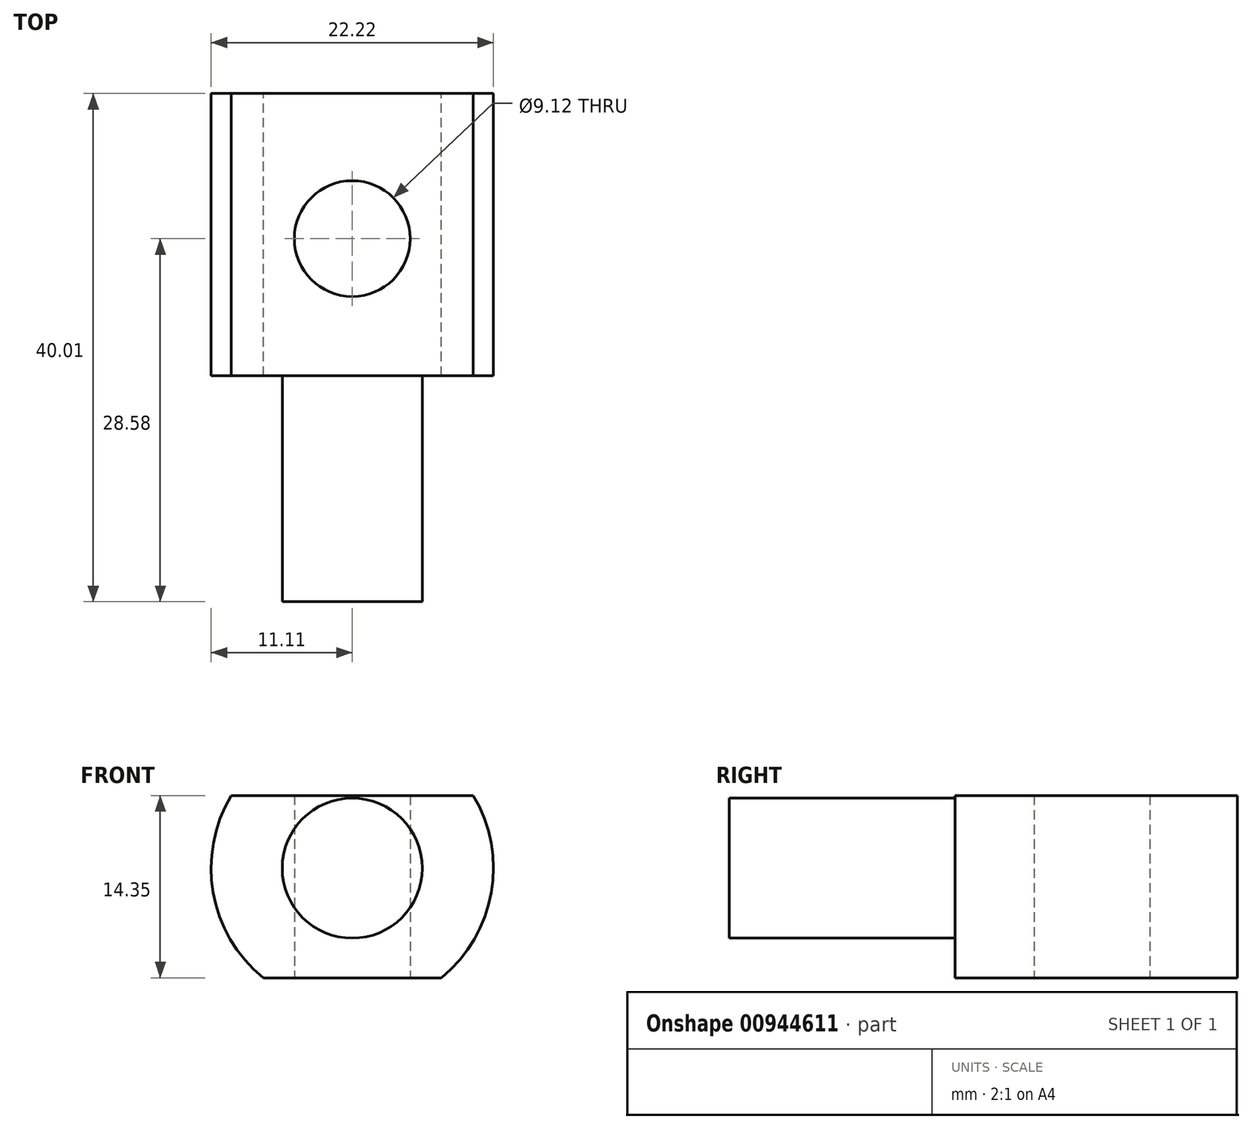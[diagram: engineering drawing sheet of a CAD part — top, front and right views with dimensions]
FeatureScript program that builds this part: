
annotation { "Feature Type Name" : "Feature", "Feature Type Description" : "" }
export const myFeature = defineFeature(function(context is Context, id is Id, definition is map)
    precondition{}
    {
        {
            var Q0;
            Q0=qCreatedBy(makeId("Front.planeOp"),FACE);
            var sketch = newSketch(context, id + "F0", { "sketchPlane" : qUnion([Q0])});
            skLineSegment(sketch, "E0", {"start": v(9.52, 5.72) * mm, "end": v(-9.53, 5.72) * mm});
            skLineSegment(sketch, "E1", {"start": v(-7, -8.63) * mm, "end": v(7, -8.63) * mm});
            skArc(sketch, "E2", {"start": v(7, -8.63) * mm, "mid": v(10.94, -1.92) * mm, "end": v(9.53, 5.72) * mm});
            skArc(sketch, "E3", {"start": v(-9.53, 5.72) * mm, "mid": v(-10.94, -1.92) * mm, "end": v(-7, -8.63) * mm});
            skSolve(sketch);
        }
        {
            var Q0;
            Q0=makeQuery(id+"F0.imprint","IMPRINT",FACE,{"disambiguationData":[TD([[makeQuery(id+"F0.imprint","IMPRINT",EDGE,{"derivedFrom":sQuery(id+"F0.wireOp",EDGE,"E0")}),1.0]])]});
            extrude(context, id + "F1", {"entities" : qUnion([Q0]), "depth" : 22.22 * mm, "offsetDistance" : 25.4 * mm});
        }
        {
            var Q0;
            Q0=makeQuery(id+"F1.opExtrude","CAP_FACE",FACE,{"disambiguationData":[OSD([sQuery(id+"F0.wireOp",EDGE,"E0"),sQuery(id+"F0.wireOp",EDGE,"E1"),sQuery(id+"F0.wireOp",EDGE,"E2"),sQuery(id+"F0.wireOp",EDGE,"E3")])],"isStart":false});
            var sketch = newSketch(context, id + "F2", { "sketchPlane" : qUnion([Q0])});
            skCircle(sketch, "E4", {"center": v(0, 0) * mm, "radius": 5.51 * mm});
            skSolve(sketch);
        }
        {
            var Q0;
            Q0=makeQuery(id+"F2.imprint","IMPRINT",FACE,{"disambiguationData":[TD([[makeQuery(id+"F2.imprint","IMPRINT",EDGE,{"derivedFrom":sQuery(id+"F2.wireOp",EDGE,"E4")}),1.0]])]});
            extrude(context, id + "F3", {"entities" : qUnion([Q0]), "operationType" : NewBodyOperationType.ADD, "depth" : 17.78 * mm, "offsetDistance" : 25.4 * mm});
        }
        {
            var Q0;
            Q0=makeQuery(id+"F1.opExtrude","SWEPT_FACE",FACE,{"disambiguationData":[OSD([sQuery(id+"F0.wireOp",EDGE,"E1")])]});
            var sketch = newSketch(context, id + "F4", { "sketchPlane" : qUnion([Q0])});
            skPoint(sketch, "E5", {"position": v(0, 11.43) * mm});
            skSolve(sketch);
        }
        {
            var Q0;
            Q0=sQuery(id+"F4.wireOp",VERTEX,"E5");
            var Q1;
            Q1=makeQuery(id+"F1.opExtrude","SWEPT_BODY",BODY,{"disambiguationData":[OSD([sQuery(id+"F0.wireOp",EDGE,"E0"),sQuery(id+"F0.wireOp",EDGE,"E1"),sQuery(id+"F0.wireOp",EDGE,"E2"),sQuery(id+"F0.wireOp",EDGE,"E3")])]});
            hole(context, id + "F5", {"style" : HoleStyle.SIMPLE, "endStyle" : HoleEndStyle.THROUGH, "standardTappedOrClearance" : lookupTablePath({ "fit" : "Loose (ASME)", "standard" : "ANSI", "size" : "5/16", "type" : "Clearance" }), "standardBlindInLast" : lookupTablePath({ "fit" : "Loose", "standard" : "ANSI", "engagement" : "75%", "pitch" : "18 tpi", "size" : "5/16", "type" : "Clearance & tapped" }), "holeDiameter" : 9.12 * mm, "majorDiameter" : 7.94 * mm, "tappedDepth" : 10.3 * mm, "tapClearance" : 3, "locations" : qUnion([Q0]), "scope" : qUnion([Q1])});
        }
    });
